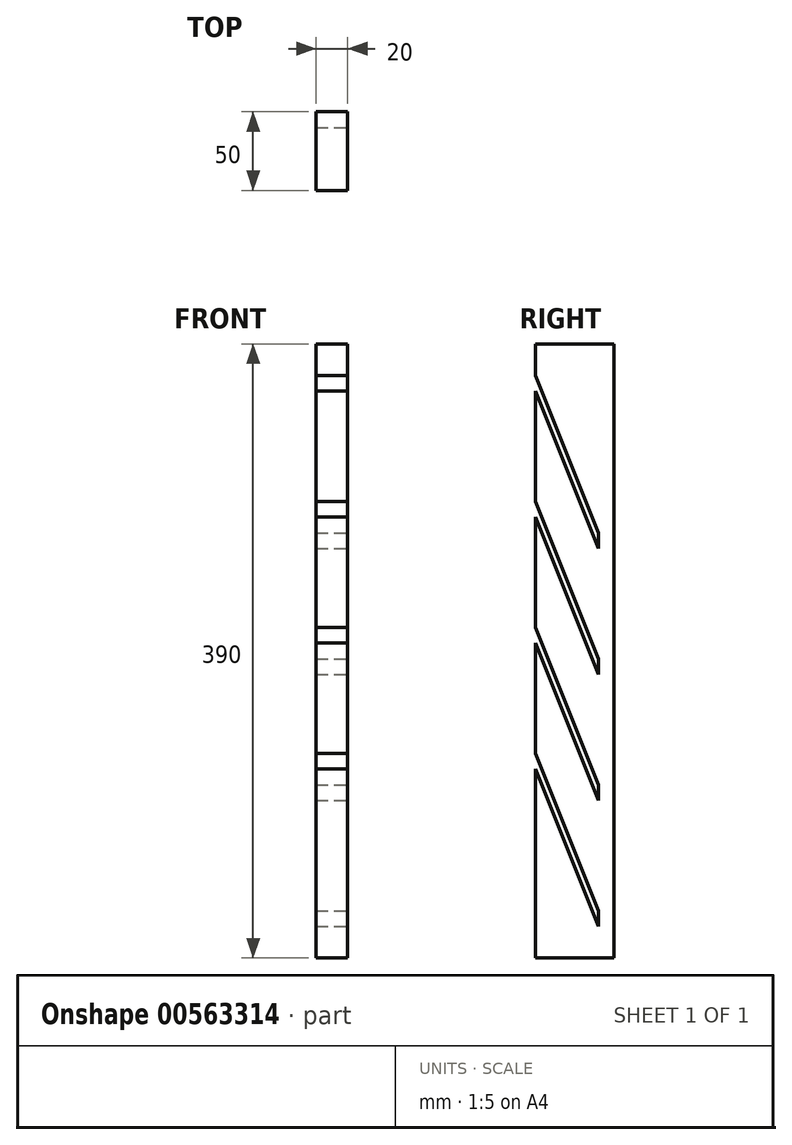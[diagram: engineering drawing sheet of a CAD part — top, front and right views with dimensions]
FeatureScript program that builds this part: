
annotation { "Feature Type Name" : "Feature", "Feature Type Description" : "" }
export const myFeature = defineFeature(function(context is Context, id is Id, definition is map)
    precondition{}
    {
        {
            var Q0;
            Q0=qCreatedBy(makeId("Right.planeOp"),FACE);
            var sketch = newSketch(context, id + "F0", { "sketchPlane" : qUnion([Q0])});
            skLineSegment(sketch, "E0.bottom", {"start": v(-65.52, 319.1) * mm, "end": v(-15.52, 319.1) * mm});
            skLineSegment(sketch, "E0.top", {"start": v(-65.52, -70.9) * mm, "end": v(-15.52, -70.9) * mm});
            skLineSegment(sketch, "E0.left", {"start": v(-65.52, 319.1) * mm, "end": v(-65.52, -70.9) * mm});
            skLineSegment(sketch, "E0.right", {"start": v(-15.52, 319.1) * mm, "end": v(-15.52, -70.9) * mm});
            skSolve(sketch);
        }
        {
            var Q0;
            Q0 = qSketchRegion(id + "F0", true);
            extrude(context, id + "F1", {"entities" : qUnion([Q0]), "depth" : 20 * mm, "offsetDistance" : 25 * mm});
        }
        {
            var Q0;
            Q0=makeQuery(id+"F1.opExtrude","CAP_FACE",FACE,{"disambiguationData":[OSD([sQuery(id+"F0.wireOp",EDGE,"E0.bottom"),sQuery(id+"F0.wireOp",EDGE,"E0.top"),sQuery(id+"F0.wireOp",EDGE,"E0.left"),sQuery(id+"F0.wireOp",EDGE,"E0.right")])],"isStart":false});
            var sketch = newSketch(context, id + "F2", { "sketchPlane" : qUnion([Q0])});
            skLineSegment(sketch, "E1", {"start": v(-65.52, 49.1) * mm, "end": v(-25.52, -50.9) * mm});
            skLineSegment(sketch, "E2", {"start": v(-25.52, -50.9) * mm, "end": v(-25.52, -40.9) * mm});
            skLineSegment(sketch, "E3", {"start": v(-25.52, -40.9) * mm, "end": v(-65.52, 59.1) * mm});
            skLineSegment(sketch, "E4", {"start": v(-65.52, 59.1) * mm, "end": v(-65.52, 49.1) * mm});
            skLineSegment(sketch, "E5.0.1.0", {"start": v(-25.52, 39.1) * mm, "end": v(-65.52, 139.1) * mm});
            skLineSegment(sketch, "E5.0.1.1", {"start": v(-65.52, 129.1) * mm, "end": v(-25.52, 29.1) * mm});
            skLineSegment(sketch, "E5.0.1.2", {"start": v(-65.52, 139.1) * mm, "end": v(-65.52, 129.1) * mm});
            skLineSegment(sketch, "E5.0.1.3", {"start": v(-25.52, 29.1) * mm, "end": v(-25.52, 39.1) * mm});
            skLineSegment(sketch, "E5.0.2.0", {"start": v(-25.52, 119.1) * mm, "end": v(-65.52, 219.1) * mm});
            skLineSegment(sketch, "E5.0.2.1", {"start": v(-65.52, 209.1) * mm, "end": v(-25.52, 109.1) * mm});
            skLineSegment(sketch, "E5.0.2.2", {"start": v(-65.52, 219.1) * mm, "end": v(-65.52, 209.1) * mm});
            skLineSegment(sketch, "E5.0.2.3", {"start": v(-25.52, 109.1) * mm, "end": v(-25.52, 119.1) * mm});
            skLineSegment(sketch, "E5.0.3.0", {"start": v(-25.52, 199.1) * mm, "end": v(-65.52, 299.1) * mm});
            skLineSegment(sketch, "E5.0.3.1", {"start": v(-65.52, 289.1) * mm, "end": v(-25.52, 189.1) * mm});
            skLineSegment(sketch, "E5.0.3.2", {"start": v(-65.52, 299.1) * mm, "end": v(-65.52, 289.1) * mm});
            skLineSegment(sketch, "E5.0.3.3", {"start": v(-25.52, 189.1) * mm, "end": v(-25.52, 199.1) * mm});
            skLineSegment(sketch, "E5.direction1", {"start": v(-25.52, -40.9) * mm, "end": v(-0.52, -40.9) * mm, "construction": true});
            skLineSegment(sketch, "E5.direction2", {"start": v(-25.52, -40.9) * mm, "end": v(-25.52, 39.1) * mm, "construction": true});
            skSolve(sketch);
        }
        {
            var Q0;
            Q0 = qSketchRegion(id + "F2", true);
            extrude(context, id + "F3", {"entities" : qUnion([Q0]), "operationType" : NewBodyOperationType.REMOVE, "endBound" : BoundingType.THROUGH_ALL, "oppositeDirection" : true, "depth" : 25 * mm, "offsetDistance" : 25 * mm});
        }
    });
